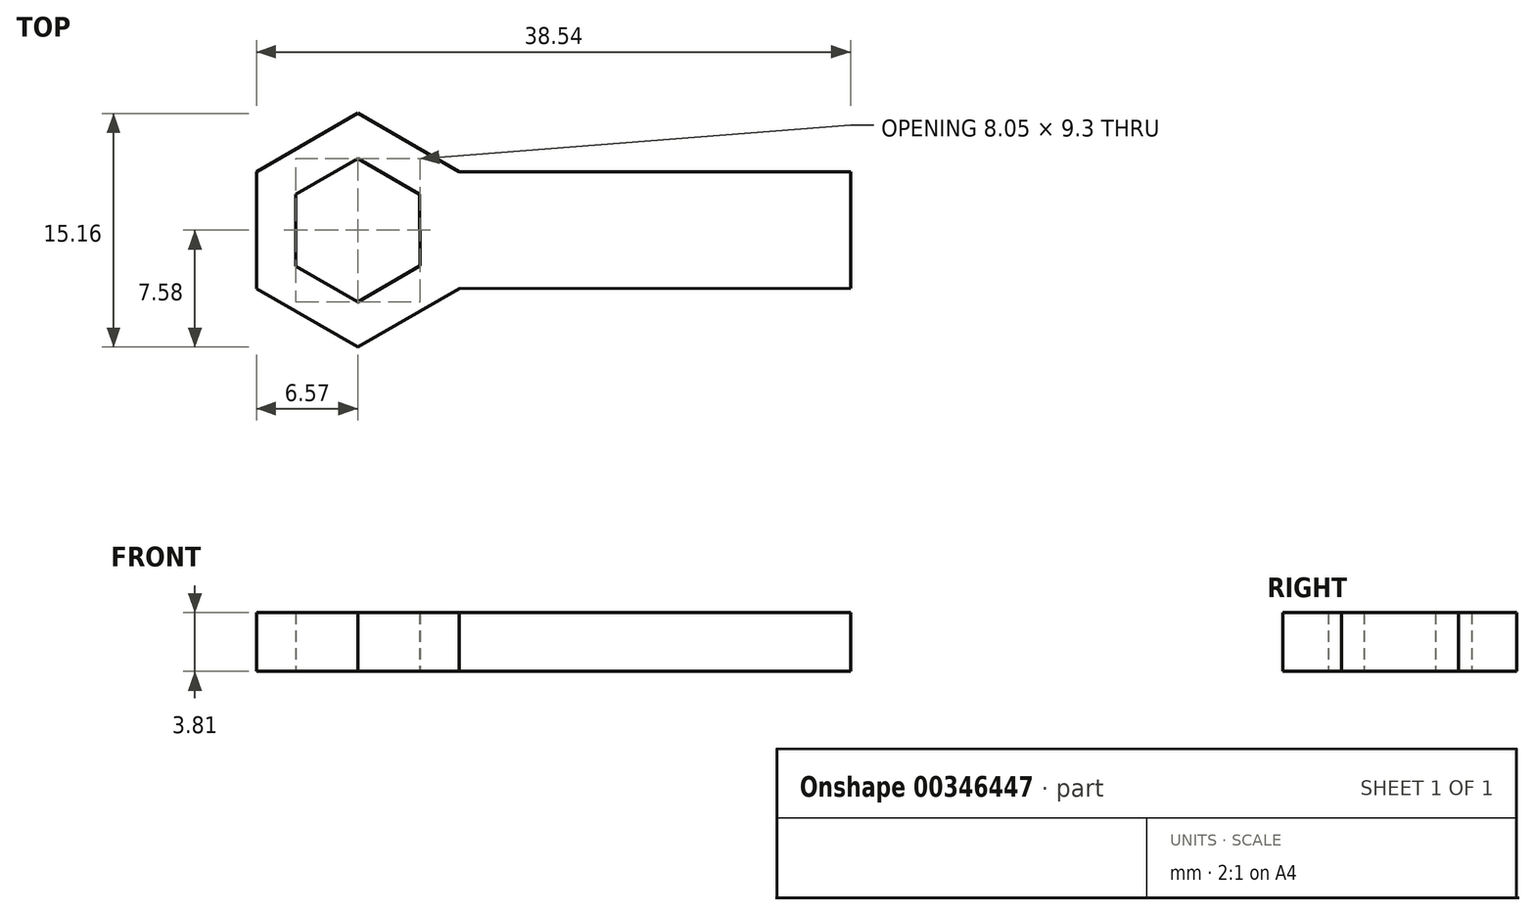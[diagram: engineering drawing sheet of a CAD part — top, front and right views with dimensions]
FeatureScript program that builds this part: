
annotation { "Feature Type Name" : "Feature", "Feature Type Description" : "" }
export const myFeature = defineFeature(function(context is Context, id is Id, definition is map)
    precondition{}
    {
        {
            var Q0;
            Q0=qCreatedBy(makeId("Top.planeOp"),FACE);
            var sketch = newSketch(context, id + "F0", { "sketchPlane" : qUnion([Q0])});
            skCircle(sketch, "E0.cCircle", {"center": v(0, 0) * mm, "radius": 4.03 * mm, "construction": true});
            skLineSegment(sketch, "E0.0", {"start": v(0, 4.65) * mm, "end": v(4.02, 2.33) * mm});
            skLineSegment(sketch, "E0.1", {"start": v(4.02, 2.33) * mm, "end": v(4.03, -2.32) * mm});
            skLineSegment(sketch, "E0.2", {"start": v(4.03, -2.32) * mm, "end": v(0, -4.65) * mm});
            skLineSegment(sketch, "E0.3", {"start": v(0, -4.65) * mm, "end": v(-4.02, -2.33) * mm});
            skLineSegment(sketch, "E0.4", {"start": v(-4.02, -2.33) * mm, "end": v(-4.03, 2.32) * mm});
            skLineSegment(sketch, "E0.5", {"start": v(-4.03, 2.32) * mm, "end": v(0, 4.65) * mm});
            skPoint(sketch, "E0.0.midPoint", {"position": v(2.01, 3.49) * mm});
            skCircle(sketch, "E1.cCircle", {"center": v(0, 0) * mm, "radius": 6.57 * mm, "construction": true});
            skLineSegment(sketch, "E1.0", {"start": v(0, 7.58) * mm, "end": v(6.56, 3.8) * mm});
            skLineSegment(sketch, "E1.1", {"start": v(6.56, 3.8) * mm, "end": v(6.57, -3.79) * mm});
            skLineSegment(sketch, "E1.2", {"start": v(6.57, -3.79) * mm, "end": v(0, -7.58) * mm});
            skLineSegment(sketch, "E1.3", {"start": v(0, -7.58) * mm, "end": v(-6.56, -3.8) * mm});
            skLineSegment(sketch, "E1.4", {"start": v(-6.56, -3.8) * mm, "end": v(-6.57, 3.79) * mm});
            skLineSegment(sketch, "E1.5", {"start": v(-6.57, 3.79) * mm, "end": v(0, 7.58) * mm});
            skPoint(sketch, "E1.0.midPoint", {"position": v(3.28, 5.69) * mm});
            skSolve(sketch);
        }
        {
            var Q0;
            Q0=qSketchRegion(id+"F0",true);
            extrude(context, id + "F1", {"entities" : qUnion([Q0]), "depth" : 3.8 * mm});
        }
        {
            var Q0;
            Q0=makeQuery(id+"F1.opExtrude","SWEPT_FACE",FACE,{"disambiguationData":[OSD([sQuery(id+"F0.wireOp",EDGE,"E1.1")])]});
            extrude(context, id + "F2", {"entities" : qUnion([Q0]), "operationType" : NewBodyOperationType.ADD, "depth" : 25.4 * mm});
        }
    });
